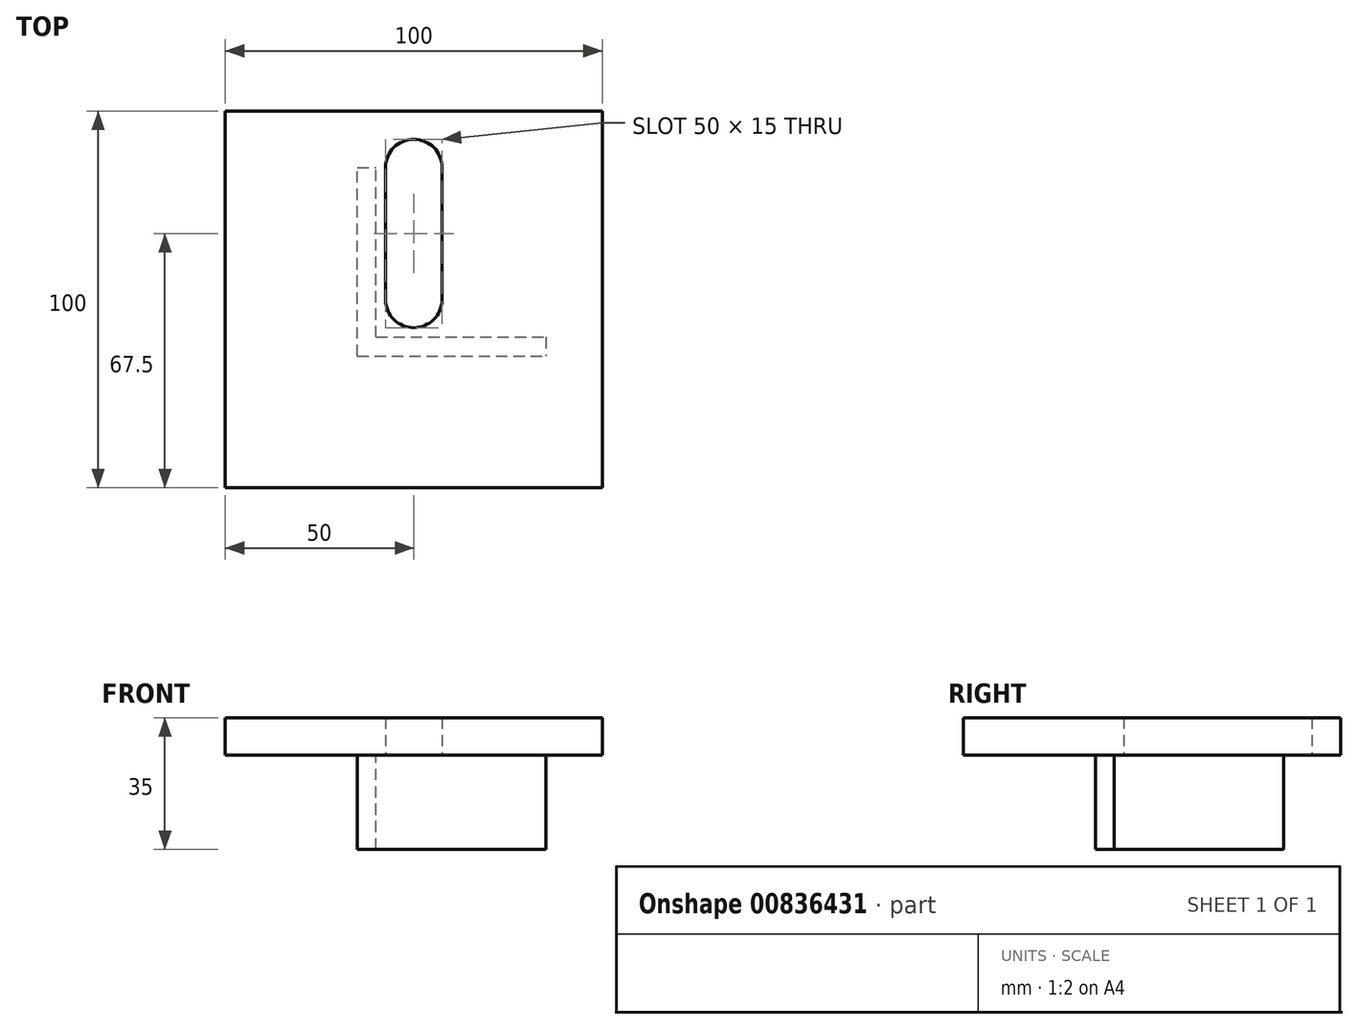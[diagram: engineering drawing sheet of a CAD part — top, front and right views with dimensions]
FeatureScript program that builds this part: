
annotation { "Feature Type Name" : "Feature", "Feature Type Description" : "" }
export const myFeature = defineFeature(function(context is Context, id is Id, definition is map)
    precondition{}
    {
        {
            var Q0;
            Q0=qCreatedBy(makeId("Top.planeOp"),FACE);
            var sketch = newSketch(context, id + "F0", { "sketchPlane" : qUnion([Q0])});
            skLineSegment(sketch, "E0.bottom", {"start": v(-50, -50) * mm, "end": v(50, -50) * mm});
            skLineSegment(sketch, "E0.top", {"start": v(-50, 50) * mm, "end": v(50, 50) * mm});
            skLineSegment(sketch, "E0.left", {"start": v(-50, -50) * mm, "end": v(-50, 50) * mm});
            skLineSegment(sketch, "E0.right", {"start": v(50, -50) * mm, "end": v(50, 50) * mm});
            skSolve(sketch);
        }
        {
            var Q0;
            Q0=makeQuery(id+"F0.imprint","IMPRINT",FACE,{"disambiguationData":[TD([[makeQuery(id+"F0.imprint","IMPRINT",EDGE,{"derivedFrom":sQuery(id+"F0.wireOp",EDGE,"E0.bottom")}),1.0]])]});
            extrude(context, id + "F1", {"entities" : qUnion([Q0]), "depth" : 10 * mm, "offsetDistance" : 25 * mm});
        }
        {
            var Q0;
            Q0=qCreatedBy(makeId("Top.planeOp"),FACE);
            var sketch = newSketch(context, id + "F2", { "sketchPlane" : qUnion([Q0])});
            skLineSegment(sketch, "E1.bottom", {"start": v(-10, -10) * mm, "end": v(35, -10) * mm});
            skLineSegment(sketch, "E1.left", {"start": v(-10, -10) * mm, "end": v(-10, 35) * mm});
            skLineSegment(sketch, "E2.0", {"start": v(-15, -15) * mm, "end": v(-15, 35) * mm});
            skLineSegment(sketch, "E2.1", {"start": v(-15, -15) * mm, "end": v(35, -15) * mm});
            skLineSegment(sketch, "E3.0", {"start": v(45, 45) * mm, "end": v(-45, 45) * mm});
            skLineSegment(sketch, "E3.1", {"start": v(45, -45) * mm, "end": v(45, 45) * mm});
            skLineSegment(sketch, "E3.2", {"start": v(-45, -45) * mm, "end": v(45, -45) * mm});
            skLineSegment(sketch, "E3.3", {"start": v(-45, 45) * mm, "end": v(-45, -45) * mm});
            skLineSegment(sketch, "E4", {"start": v(-15, 35) * mm, "end": v(-10, 35) * mm});
            skLineSegment(sketch, "E5", {"start": v(35, -10) * mm, "end": v(35, -15) * mm});
            skCircle(sketch, "E6", {"center": v(0, 0) * mm, "radius": 7.5 * mm});
            skSolve(sketch);
        }
        {
            var Q0;
            Q0=makeQuery(id+"F2.imprint","IMPRINT",FACE,{"disambiguationData":[TD([[makeQuery(id+"F2.imprint","IMPRINT",EDGE,{"derivedFrom":sQuery(id+"F2.wireOp",EDGE,"E1.bottom")}),-1.0]])]});
            extrude(context, id + "F3", {"entities" : qUnion([Q0]), "operationType" : NewBodyOperationType.ADD, "depth" : -25 * mm, "offsetDistance" : 25 * mm});
        }
        {
            var Q0;
            Q0=qCreatedBy(makeId("Top.planeOp"),FACE);
            var sketch = newSketch(context, id + "F4", { "sketchPlane" : qUnion([Q0])});
            skCircle(sketch, "E7", {"center": v(0, 0) * mm, "radius": 7.5 * mm});
            skCircle(sketch, "E8", {"center": v(0, 35) * mm, "radius": 7.5 * mm});
            skLineSegment(sketch, "E9", {"start": v(-7.5, 0) * mm, "end": v(-7.5, 35) * mm});
            skLineSegment(sketch, "E10", {"start": v(7.5, 0) * mm, "end": v(7.5, 35) * mm});
            skSolve(sketch);
        }
        {
            var Q0;
            {var subQ0=sQuery(id+"F4.wireOp",EDGE,"E7");var subQ1=makeQuery(id+"F4.imprint","INTERSECT",VERTEX,{"derivedFrom":[subQ0,sQuery(id+"F4.wireOp",EDGE,"E9")]});Q0=makeQuery(id+"F4.imprint","IMPRINT",FACE,{"disambiguationData":[TD([[makeQuery(id+"F4.imprint","IMPRINT",EDGE,{"disambiguationData":[TD([[subQ1,1.0]])],"derivedFrom":subQ0}),1.0]])]});}
            var Q1;
            {var subQ0=sQuery(id+"F4.wireOp",EDGE,"E9");Q1=makeQuery(id+"F4.imprint","IMPRINT",FACE,{"disambiguationData":[TD([[makeQuery(id+"F4.imprint","IMPRINT",EDGE,{"derivedFrom":subQ0}),-1.0]])]});}
            var Q2;
            {var subQ0=sQuery(id+"F4.wireOp",EDGE,"E8");var subQ1=makeQuery(id+"F4.imprint","INTERSECT",VERTEX,{"derivedFrom":[subQ0,sQuery(id+"F4.wireOp",EDGE,"E9")]});Q2=makeQuery(id+"F4.imprint","IMPRINT",FACE,{"disambiguationData":[TD([[makeQuery(id+"F4.imprint","IMPRINT",EDGE,{"disambiguationData":[TD([[subQ1,1.0]])],"derivedFrom":subQ0}),1.0]])]});}
            extrude(context, id + "F5", {"entities" : qUnion([Q0, Q1, Q2]), "operationType" : NewBodyOperationType.REMOVE, "oppositeDirection" : true, "depth" : -25 * mm, "offsetDistance" : 25 * mm});
        }
    });
